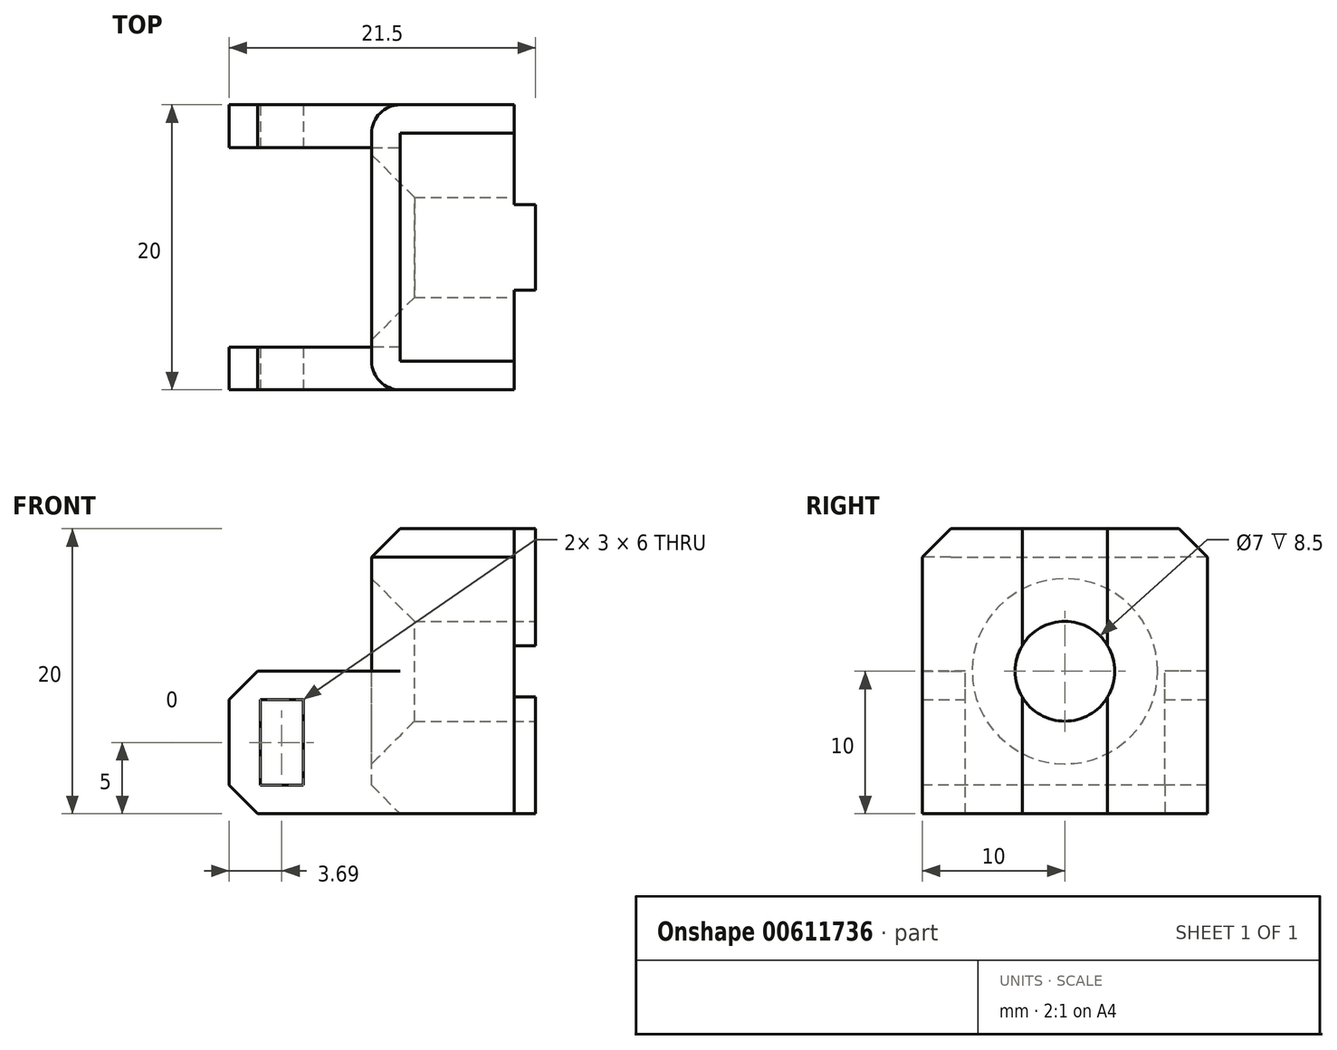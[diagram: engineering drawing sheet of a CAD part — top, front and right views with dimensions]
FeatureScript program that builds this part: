
annotation { "Feature Type Name" : "Feature", "Feature Type Description" : "" }
export const myFeature = defineFeature(function(context is Context, id is Id, definition is map)
    precondition{}
    {
        {
            var Q0;
            Q0=qCreatedBy(makeId("Top.planeOp"),FACE);
            var sketch = newSketch(context, id + "F0", { "sketchPlane" : qUnion([Q0])});
            skLineSegment(sketch, "E0.bottom", {"start": v(-5, 10) * mm, "end": v(5, 10) * mm});
            skLineSegment(sketch, "E0.top", {"start": v(-5, -10) * mm, "end": v(5, -10) * mm});
            skLineSegment(sketch, "E0.left", {"start": v(-5, 10) * mm, "end": v(-5, -10) * mm});
            skLineSegment(sketch, "E0.right", {"start": v(5, 10) * mm, "end": v(5, 3) * mm});
            skLineSegment(sketch, "E1.bottom", {"start": v(5, 3) * mm, "end": v(6.5, 3) * mm});
            skLineSegment(sketch, "E1.top", {"start": v(5, -3) * mm, "end": v(6.5, -3) * mm});
            skLineSegment(sketch, "E1.right", {"start": v(6.5, 3) * mm, "end": v(6.5, -3) * mm});
            skLineSegment(sketch, "E2.trimOffspring", {"start": v(5, -3) * mm, "end": v(5, -10) * mm});
            skSolve(sketch);
        }
        {
            var Q0;
            Q0=makeQuery(id+"F0.imprint","IMPRINT",FACE,{"disambiguationData":[TD([[makeQuery(id+"F0.imprint","IMPRINT",EDGE,{"derivedFrom":sQuery(id+"F0.wireOp",EDGE,"E0.bottom")}),-1.0]])]});
            extrude(context, id + "F1", {"entities" : qUnion([Q0]), "depth" : 20 * mm, "offsetDistance" : 25 * mm});
        }
        {
            var Q0;
            Q0=makeQuery(id+"F1.opExtrude","SWEPT_FACE",FACE,{"disambiguationData":[OSD([sQuery(id+"F0.wireOp",EDGE,"E1.right")])]});
            var sketch = newSketch(context, id + "F2", { "sketchPlane" : qUnion([Q0])});
            skCircle(sketch, "E3", {"center": v(0, 10) * mm, "radius": 3.5 * mm});
            skPoint(sketch, "E3.centerSnap0", {"position": v(3, 10) * mm});
            skSolve(sketch);
        }
        {
            var Q0;
            {var subQ0=sQuery(id+"F2.wireOp",EDGE,"E3");var subQ1=sQuery(id+"F0.wireOp",EDGE,"E1.right");var subQ2=makeQuery(id+"F2.imprint","INTERSECT",VERTEX,{"derivedFrom":[makeQuery(id+"F1.opExtrude","SWEPT_EDGE",EDGE,{"disambiguationData":[OSD([sQuery(id+"F0.wireOp",EDGE,"E1.bottom"),subQ1])]}),subQ0]});Q0=makeQuery(id+"F2.imprint","IMPRINT",FACE,{"disambiguationData":[TD([[makeQuery(id+"F2.imprint","IMPRINT",EDGE,{"disambiguationData":[TD([[subQ2,-1.0]])],"derivedFrom":subQ0}),1.0]])]});}
            var Q1;
            {var subQ0=sQuery(id+"F2.wireOp",EDGE,"E3");var subQ1=sQuery(id+"F0.wireOp",EDGE,"E1.right");var subQ2=makeQuery(id+"F1.opExtrude","SWEPT_EDGE",EDGE,{"disambiguationData":[OSD([sQuery(id+"F0.wireOp",EDGE,"E1.top"),subQ1])]});var subQ3=makeQuery(id+"F2.imprint","INTERSECT",VERTEX,{"disambiguationData":[OD(0.0)],"derivedFrom":[subQ2,subQ0]});Q1=makeQuery(id+"F2.imprint","IMPRINT",FACE,{"disambiguationData":[TD([[makeQuery(id+"F2.imprint","IMPRINT",EDGE,{"disambiguationData":[TD([[subQ3,1.0]])],"derivedFrom":subQ0}),1.0]])]});}
            var Q2;
            {var subQ0=sQuery(id+"F2.wireOp",EDGE,"E3");var subQ1=makeQuery(id+"F1.opExtrude","SWEPT_EDGE",EDGE,{"disambiguationData":[OSD([sQuery(id+"F0.wireOp",EDGE,"E1.top"),sQuery(id+"F0.wireOp",EDGE,"E1.right")])]});var subQ2=makeQuery(id+"F2.imprint","INTERSECT",VERTEX,{"disambiguationData":[OD(0.0)],"derivedFrom":[subQ1,subQ0]});Q2=makeQuery(id+"F2.imprint","IMPRINT",FACE,{"disambiguationData":[TD([[makeQuery(id+"F2.imprint","IMPRINT",EDGE,{"disambiguationData":[TD([[subQ2,-1.0]])],"derivedFrom":subQ0}),1.0]])]});}
            extrude(context, id + "F3", {"entities" : qUnion([Q0, Q1, Q2]), "operationType" : NewBodyOperationType.REMOVE, "oppositeDirection" : true, "depth" : 15 * mm, "offsetDistance" : 25 * mm});
        }
        {
            var Q0;
            Q0=makeQuery(id+"F3.boolean.opBoolean","INTERSECT",EDGE,{"derivedFrom":[makeQuery(id+"F1.opExtrude","SWEPT_FACE",FACE,{"disambiguationData":[OSD([sQuery(id+"F0.wireOp",EDGE,"E0.left")])]}),makeQuery(id+"F3.opExtrude","SWEPT_FACE",FACE,{"disambiguationData":[OSD([sQuery(id+"F2.wireOp",EDGE,"E3")])]})]});
            chamfer(context, id + "F4", {"entities" : qUnion([Q0]), "width" : 3 * mm, "tangentPropagation" : true});
        }
        {
            var Q0;
            Q0=makeQuery(id+"F1.opExtrude","SWEPT_FACE",FACE,{"disambiguationData":[OSD([sQuery(id+"F0.wireOp",EDGE,"E0.left")])]});
            var sketch = newSketch(context, id + "F5", { "sketchPlane" : qUnion([Q0])});
            skLineSegment(sketch, "E4.bottom", {"start": v(-10, 0) * mm, "end": v(-7, 0) * mm});
            skLineSegment(sketch, "E4.top", {"start": v(-10, 10) * mm, "end": v(-7, 10) * mm});
            skLineSegment(sketch, "E4.left", {"start": v(-10, 0) * mm, "end": v(-10, 10) * mm});
            skLineSegment(sketch, "E4.right", {"start": v(-7, 0) * mm, "end": v(-7, 10) * mm});
            skLineSegment(sketch, "E5.bottom", {"start": v(10, 0) * mm, "end": v(7, 0) * mm});
            skLineSegment(sketch, "E5.top", {"start": v(10, 10) * mm, "end": v(7, 10) * mm});
            skLineSegment(sketch, "E5.left", {"start": v(10, 0) * mm, "end": v(10, 10) * mm});
            skLineSegment(sketch, "E5.right", {"start": v(7, 0) * mm, "end": v(7, 10) * mm});
            skSolve(sketch);
        }
        {
            var Q0;
            Q0=makeQuery(id+"F5.imprint","IMPRINT",FACE,{"disambiguationData":[TD([[makeQuery(id+"F5.imprint","IMPRINT",EDGE,{"derivedFrom":sQuery(id+"F5.wireOp",EDGE,"E5.bottom")}),-1.0]])]});
            var Q1;
            Q1=makeQuery(id+"F5.imprint","IMPRINT",FACE,{"disambiguationData":[TD([[makeQuery(id+"F5.imprint","IMPRINT",EDGE,{"derivedFrom":sQuery(id+"F5.wireOp",EDGE,"E4.bottom")}),1.0]])]});
            var Q2;
            Q2=makeQuery(id+"F5.imprint","IMPRINT",FACE,{"disambiguationData":[TD([[makeQuery(id+"F5.imprint","IMPRINT",EDGE,{"derivedFrom":sQuery(id+"F5.wireOp",EDGE,"E5.bottom")}),1.0]])]});
            extrude(context, id + "F6", {"entities" : qUnion([Q0, Q1, Q2]), "operationType" : NewBodyOperationType.ADD, "depth" : 10 * mm, "offsetDistance" : 25 * mm});
        }
        {
            var Q0;
            Q0=makeQuery(id+"F6.boolean.opBoolean","MERGE",FACE,{"derivedFrom":[makeQuery(id+"F1.opExtrude","SWEPT_FACE",FACE,{"disambiguationData":[OSD([sQuery(id+"F0.wireOp",EDGE,"E0.top")])]}),makeQuery(id+"F6.opExtrude","SWEPT_FACE",FACE,{"disambiguationData":[OSD([sQuery(id+"F5.wireOp",EDGE,"E5.left")])]})]});
            var sketch = newSketch(context, id + "F7", { "sketchPlane" : qUnion([Q0])});
            skLineSegment(sketch, "E6.bottom", {"start": v(-9.8, 8) * mm, "end": v(-12.8, 8) * mm});
            skLineSegment(sketch, "E6.top", {"start": v(-9.8, 2) * mm, "end": v(-12.8, 2) * mm});
            skLineSegment(sketch, "E6.left", {"start": v(-9.8, 8) * mm, "end": v(-9.8, 2) * mm});
            skLineSegment(sketch, "E6.right", {"start": v(-12.8, 8) * mm, "end": v(-12.8, 2) * mm});
            skSolve(sketch);
        }
        {
            var Q0;
            Q0=makeQuery(id+"F7.imprint","IMPRINT",FACE,{"disambiguationData":[TD([[makeQuery(id+"F7.imprint","IMPRINT",EDGE,{"derivedFrom":sQuery(id+"F7.wireOp",EDGE,"E6.bottom")}),1.0]])]});
            extrude(context, id + "F8", {"entities" : qUnion([Q0]), "operationType" : NewBodyOperationType.REMOVE, "oppositeDirection" : true, "depth" : 25 * mm, "offsetDistance" : 25 * mm});
        }
        {
            var Q0;
            Q0=makeQuery(id+"F1.opExtrude","SWEPT_EDGE",EDGE,{"disambiguationData":[OSD([sQuery(id+"F0.wireOp",EDGE,"E0.top"),sQuery(id+"F0.wireOp",EDGE,"E0.left")])]});
            var Q1;
            Q1=makeQuery(id+"F1.opExtrude","SWEPT_EDGE",EDGE,{"disambiguationData":[OSD([sQuery(id+"F0.wireOp",EDGE,"E0.bottom"),sQuery(id+"F0.wireOp",EDGE,"E0.left")])]});
            fillet(context, id + "F9", {"entities" : qUnion([Q0, Q1]), "radius" : 2 * mm, "tangentPropagation" : true, "allowEdgeOverflow" : false});
        }
        {
            var Q0;
            Q0=makeQuery(id+"F6.opExtrude","CAP_EDGE",EDGE,{"disambiguationData":[OSD([sQuery(id+"F5.wireOp",EDGE,"E5.top")])],"isStart":false});
            var Q1;
            Q1=makeQuery(id+"F6.opExtrude","CAP_EDGE",EDGE,{"disambiguationData":[OSD([sQuery(id+"F5.wireOp",EDGE,"E4.top")])],"isStart":false});
            var Q2;
            Q2=makeQuery(id+"F6.opExtrude","CAP_EDGE",EDGE,{"disambiguationData":[OSD([sQuery(id+"F5.wireOp",EDGE,"E4.bottom")])],"isStart":false});
            var Q3;
            Q3=makeQuery(id+"F6.opExtrude","CAP_EDGE",EDGE,{"disambiguationData":[OSD([sQuery(id+"F5.wireOp",EDGE,"E5.bottom")])],"isStart":false});
            var Q4;
            Q4=makeQuery(id+"F1.opExtrude","CAP_EDGE",EDGE,{"disambiguationData":[OSD([sQuery(id+"F0.wireOp",EDGE,"E0.left")])],"isStart":true});
            var Q5;
            Q5=makeQuery(id+"F1.opExtrude","CAP_EDGE",EDGE,{"disambiguationData":[OSD([sQuery(id+"F0.wireOp",EDGE,"E0.left")])],"isStart":false});
            chamfer(context, id + "F10", {"entities" : qUnion([Q0, Q1, Q2, Q3, Q4, Q5]), "width" : 2 * mm, "tangentPropagation" : true});
        }
    });
